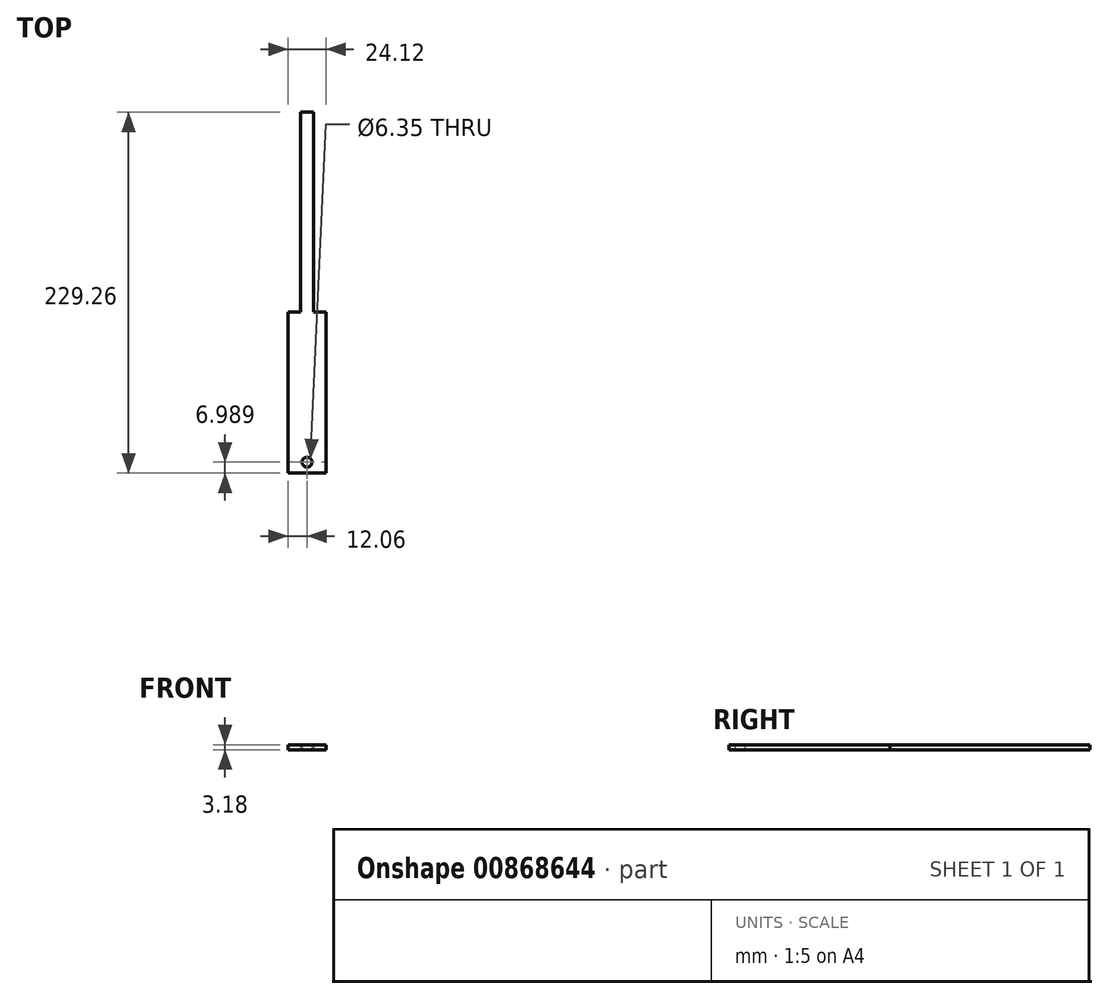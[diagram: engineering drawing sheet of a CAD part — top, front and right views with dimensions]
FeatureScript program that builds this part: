
annotation { "Feature Type Name" : "Feature", "Feature Type Description" : "" }
export const myFeature = defineFeature(function(context is Context, id is Id, definition is map)
    precondition{}
    {
        {
            var Q0;
            Q0=qCreatedBy(makeId("Top.planeOp"),FACE);
            var sketch = newSketch(context, id + "F0", { "sketchPlane" : qUnion([Q0])});
            skLineSegment(sketch, "E0.top", {"start": v(-12.07, -49.49) * mm, "end": v(12.07, -49.49) * mm});
            skLineSegment(sketch, "E0.left", {"start": v(-12.06, 52.77) * mm, "end": v(-12.07, -49.49) * mm});
            skLineSegment(sketch, "E0.right", {"start": v(12.07, 52.77) * mm, "end": v(12.06, -49.49) * mm});
            skLineSegment(sketch, "E1.top", {"start": v(-4.2, 179.77) * mm, "end": v(4.2, 179.77) * mm});
            skLineSegment(sketch, "E1.left", {"start": v(-4.2, 52.77) * mm, "end": v(-4.2, 179.77) * mm});
            skLineSegment(sketch, "E1.right", {"start": v(4.2, 52.77) * mm, "end": v(4.2, 179.77) * mm});
            skLineSegment(sketch, "E2", {"start": v(-12.06, 52.77) * mm, "end": v(-4.2, 52.77) * mm});
            skLineSegment(sketch, "E3", {"start": v(4.2, 52.77) * mm, "end": v(12.07, 52.77) * mm});
            skLineSegment(sketch, "E4", {"start": v(0, 179.77) * mm, "end": v(0, -52.61) * mm, "construction": true});
            skCircle(sketch, "E5", {"center": v(0, -42.5) * mm, "radius": 3.18 * mm});
            skLineSegment(sketch, "E6", {"start": v(-4.2, 67.06) * mm, "end": v(4.2, 67.06) * mm, "construction": true});
            skSolve(sketch);
        }
        {
            var Q0;
            Q0=makeQuery(id+"F0.imprint","IMPRINT",FACE,{"disambiguationData":[TD([[makeQuery(id+"F0.imprint","IMPRINT",EDGE,{"derivedFrom":sQuery(id+"F0.wireOp",EDGE,"E0.top")}),1.0]])]});
            extrude(context, id + "F1", {"entities" : qUnion([Q0]), "depth" : 3.17 * mm, "offsetDistance" : 25.4 * mm});
        }
    });
